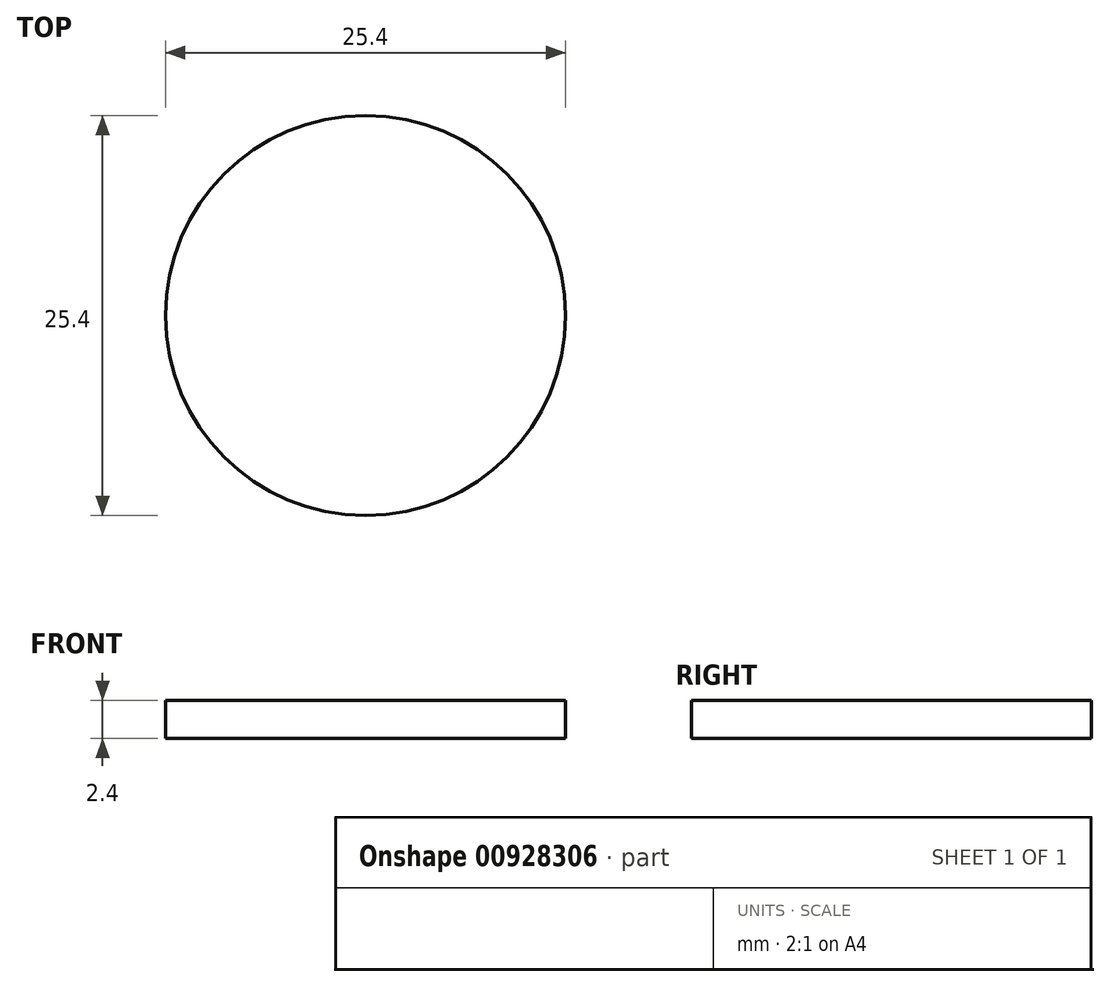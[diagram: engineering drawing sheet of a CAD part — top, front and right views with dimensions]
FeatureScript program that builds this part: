
annotation { "Feature Type Name" : "Feature", "Feature Type Description" : "" }
export const myFeature = defineFeature(function(context is Context, id is Id, definition is map)
    precondition{}
    {
        {
            var Q0;
            Q0=qCreatedBy(makeId("Top.planeOp"),FACE);
            var sketch = newSketch(context, id + "F0", { "sketchPlane" : qUnion([Q0])});
            skCircle(sketch, "E0", {"center": v(0, 0) * mm, "radius": 12.7 * mm});
            skSolve(sketch);
        }
        {
            var Q0;
            Q0=makeQuery(id+"F0.imprint","IMPRINT",FACE,{"disambiguationData":[TD([[makeQuery(id+"F0.imprint","IMPRINT",EDGE,{"derivedFrom":sQuery(id+"F0.wireOp",EDGE,"E0")}),1.0]])]});
            extrude(context, id + "F1", {"entities" : qUnion([Q0]), "depth" : 2.4 * mm, "offsetDistance" : 25 * mm});
        }
    });
